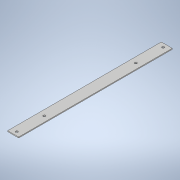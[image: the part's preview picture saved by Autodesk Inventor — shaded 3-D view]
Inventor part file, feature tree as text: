
AUTODESK INVENTOR PART (.ipt)
format: ipt  version: 2021 (Build 250183000, 183)  size: 114,176 bytes
history: native  units: in
note: dims shown in document units (in); Inventor stores cm internally (conversion verified against a paired STEP export)
features: extrude x2, sketch x2
ambient origin geometry x8: Origin, YZ Plane, XZ Plane, XY Plane, X Axis, Y Axis, Z Axis, Center Point
bodies: Solid1 (feature_tree)
feature tree (4):
  extrude  "Extrusion1"  Depth=21.0in
  extrude  "Extrusion2"  Depth=0.125in
  sketch  "Sketch1"  dims[d0=1.5in d1=21.0in]
  sketch  "Sketch2"  dims[d2=0.125in d3=0.0in d5=0.3125in d7=0.3125in d10=0.3125in d11=0.3125in d12=1.0in d13=0.0in d14=0.5in d15=4.25in d16=0.5in d17=4.25in]
